# Revit family: Lighting - Auberge Double Candelabra
name_source: partatom
category: Lighting Fixtures
revit_build: Autodesk Revit 2018 (Build: 20170927_1515(x64)
units: mm (PartAtom-declared; Revit-internal decimal feet)

## family parameters
Always vertical = Yes
Cut with Voids When Loaded = No
Host = Wall
Light Source = No
OmniClass Number = 23.80.70.00
OmniClass Title = Lighting
Part Type = Normal
Room Calculation Point = No
Round Connector Dimension = Use Diameter
Shared = No

## types (3) — shared parameters
Apparent Load = 20 VA
Description = LED Candelabra Wall Sconce
Keynote = X
Lamp = 2x 10W LED
Manufacturer = Auberge Lighting
Shade Tag = CO-7W7H
URL = https://www.aubergelighting.com

## per-type parameters (varying)
| type | Bracket Finish | Model | Shade Finish |
| Island Breeze & Brass | AU Enviro Satin Brass | AU-C10W-30-8-CO7W7H-IB-DE2A-ESB | AU Island Breeze |
| Linear Cross & Bronze | AU Enviro Bronze | AU-C10W-30-8-CO7W7H-LCV-DE2A-E0B | AU Linear Cross |
| Rain & Nickel | AU Enviro Satin Nickel | AU-C10W-30-8-CO7W7H-RV-DE2A-ESN | AU Rain |

## geometry (parser evidence)
native form markers: Sweep x12
no freeform markers — native parametric forms only
